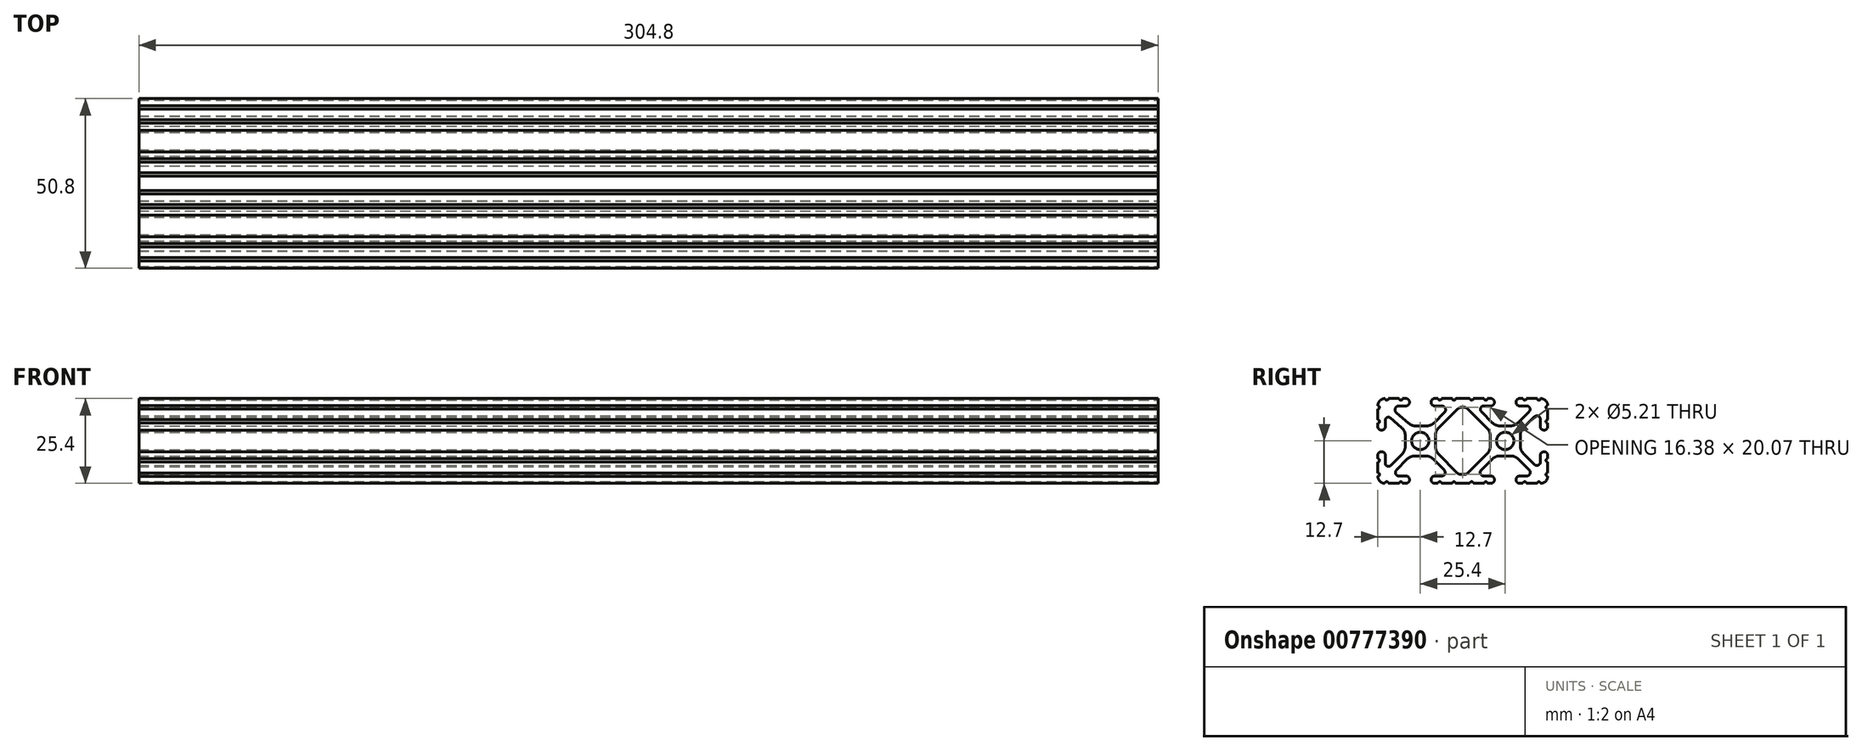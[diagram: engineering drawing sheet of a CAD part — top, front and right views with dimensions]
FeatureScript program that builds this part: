
annotation { "Feature Type Name" : "Feature", "Feature Type Description" : "" }
export const myFeature = defineFeature(function(context is Context, id is Id, definition is map)
    precondition{}
    {
        {
            var Q0;
            Q0=qCreatedBy(makeId("Right.planeOp"),FACE);
            var sketch = newSketch(context, id + "F0", { "sketchPlane" : qUnion([Q0])});
            skLineSegment(sketch, "E0", {"start": v(7.26, 3.87) * mm, "end": v(1.55, 9.57) * mm});
            skArc(sketch, "E1", {"start": v(1.55, 9.57) * mm, "mid": v(1.04, 9.91) * mm, "end": v(0.43, 10.03) * mm});
            skLineSegment(sketch, "E2", {"start": v(0.43, 10.03) * mm, "end": v(-0.43, 10.03) * mm});
            skArc(sketch, "E3", {"start": v(-0.43, 10.03) * mm, "mid": v(-1.04, 9.91) * mm, "end": v(-1.55, 9.57) * mm});
            skLineSegment(sketch, "E4", {"start": v(-1.55, 9.57) * mm, "end": v(-7.26, 3.87) * mm});
            skArc(sketch, "E5", {"start": v(-7.26, 3.87) * mm, "mid": v(-7.95, 2.84) * mm, "end": v(-8.2, 1.62) * mm});
            skLineSegment(sketch, "E6", {"start": v(-8.2, 1.62) * mm, "end": v(-8.2, -1.62) * mm});
            skLineSegment(sketch, "E7", {"start": v(-7.28, -3.85) * mm, "end": v(-1.68, -9.56) * mm});
            skArc(sketch, "E8", {"start": v(-1.68, -9.56) * mm, "mid": v(-1.16, -9.91) * mm, "end": v(-0.55, -10.03) * mm});
            skLineSegment(sketch, "E9", {"start": v(-0.55, -10.03) * mm, "end": v(0.4, -10.03) * mm});
            skArc(sketch, "E10", {"start": v(0.4, -10.03) * mm, "mid": v(1, -9.91) * mm, "end": v(1.5, -9.58) * mm});
            skLineSegment(sketch, "E11", {"start": v(1.5, -9.58) * mm, "end": v(7.25, -3.88) * mm});
            skArc(sketch, "E12", {"start": v(7.25, -3.88) * mm, "mid": v(7.95, -2.84) * mm, "end": v(8.2, -1.62) * mm});
            skLineSegment(sketch, "E13", {"start": v(8.2, -1.62) * mm, "end": v(8.2, 1.62) * mm});
            skArc(sketch, "E14", {"start": v(8.2, 1.62) * mm, "mid": v(7.95, 2.84) * mm, "end": v(7.26, 3.87) * mm});
            skCircle(sketch, "E15", {"center": v(12.7, 0) * mm, "radius": 2.6 * mm});
            skCircle(sketch, "E16", {"center": v(-12.7, 0) * mm, "radius": 2.6 * mm});
            skArc(sketch, "E17", {"start": v(-8.2, -1.62) * mm, "mid": v(-7.96, -2.82) * mm, "end": v(-7.28, -3.85) * mm});
            skLineSegment(sketch, "E18", {"start": v(-15.94, -11.65) * mm, "end": v(-15.94, -11.54) * mm});
            skArc(sketch, "E19", {"start": v(-15.94, -11.54) * mm, "mid": v(-16.25, -10.8) * mm, "end": v(-16.99, -10.5) * mm});
            skLineSegment(sketch, "E20", {"start": v(-16.99, -10.5) * mm, "end": v(-19.12, -10.5) * mm});
            skArc(sketch, "E21", {"start": v(-19.84, -8.77) * mm, "mid": v(-20.05, -9.87) * mm, "end": v(-19.12, -10.5) * mm});
            skLineSegment(sketch, "E22", {"start": v(-19.84, -8.77) * mm, "end": v(-16.62, -5.46) * mm});
            skArc(sketch, "E23", {"start": v(-14.34, -4.5) * mm, "mid": v(-15.58, -4.75) * mm, "end": v(-16.62, -5.46) * mm});
            skLineSegment(sketch, "E24", {"start": v(-14.34, -4.5) * mm, "end": v(-11.08, -4.5) * mm});
            skArc(sketch, "E25", {"start": v(-8.82, -5.45) * mm, "mid": v(-9.85, -4.74) * mm, "end": v(-11.08, -4.5) * mm});
            skLineSegment(sketch, "E26", {"start": v(-8.82, -5.45) * mm, "end": v(-5.56, -8.76) * mm});
            skArc(sketch, "E27", {"start": v(-6.29, -10.5) * mm, "mid": v(-5.35, -9.87) * mm, "end": v(-5.56, -8.76) * mm});
            skLineSegment(sketch, "E28", {"start": v(-6.29, -10.5) * mm, "end": v(-8.41, -10.5) * mm});
            skArc(sketch, "E29", {"start": v(-8.41, -10.5) * mm, "mid": v(-9.15, -10.8) * mm, "end": v(-9.46, -11.54) * mm});
            skLineSegment(sketch, "E30", {"start": v(-9.46, -11.54) * mm, "end": v(-9.46, -11.65) * mm});
            skArc(sketch, "E31", {"start": v(-9.46, -11.65) * mm, "mid": v(-9.15, -12.4) * mm, "end": v(-8.41, -12.7) * mm});
            skLineSegment(sketch, "E32", {"start": v(-8.41, -12.7) * mm, "end": v(-7.38, -12.7) * mm});
            skArc(sketch, "E33", {"start": v(-6.37, -12.7) * mm, "mid": v(-6.87, -12.2) * mm, "end": v(-7.38, -12.7) * mm});
            skLineSegment(sketch, "E34", {"start": v(-6.37, -12.7) * mm, "end": v(-3.15, -12.7) * mm});
            skArc(sketch, "E35", {"start": v(-2.13, -12.7) * mm, "mid": v(-2.64, -12.2) * mm, "end": v(-3.15, -12.7) * mm});
            skLineSegment(sketch, "E36", {"start": v(-2.13, -12.7) * mm, "end": v(2.13, -12.7) * mm});
            skArc(sketch, "E37", {"start": v(3.15, -12.7) * mm, "mid": v(2.64, -12.2) * mm, "end": v(2.13, -12.7) * mm});
            skLineSegment(sketch, "E38", {"start": v(3.15, -12.7) * mm, "end": v(6.37, -12.7) * mm});
            skArc(sketch, "E39", {"start": v(7.38, -12.7) * mm, "mid": v(6.87, -12.2) * mm, "end": v(6.37, -12.7) * mm});
            skLineSegment(sketch, "E40", {"start": v(7.38, -12.7) * mm, "end": v(8.41, -12.7) * mm});
            skArc(sketch, "E41", {"start": v(8.41, -12.7) * mm, "mid": v(9.15, -12.4) * mm, "end": v(9.46, -11.65) * mm});
            skLineSegment(sketch, "E42", {"start": v(9.46, -11.65) * mm, "end": v(9.46, -11.54) * mm});
            skArc(sketch, "E43", {"start": v(9.46, -11.54) * mm, "mid": v(9.15, -10.8) * mm, "end": v(8.41, -10.5) * mm});
            skLineSegment(sketch, "E44", {"start": v(8.41, -10.5) * mm, "end": v(6.28, -10.5) * mm});
            skArc(sketch, "E45", {"start": v(5.53, -8.67) * mm, "mid": v(5.3, -9.83) * mm, "end": v(6.28, -10.5) * mm});
            skLineSegment(sketch, "E46", {"start": v(5.53, -8.67) * mm, "end": v(8.8, -5.42) * mm});
            skArc(sketch, "E47", {"start": v(11.05, -4.5) * mm, "mid": v(9.84, -4.73) * mm, "end": v(8.8, -5.42) * mm});
            skLineSegment(sketch, "E48", {"start": v(11.05, -4.5) * mm, "end": v(14.35, -4.5) * mm});
            skArc(sketch, "E49", {"start": v(16.6, -5.42) * mm, "mid": v(15.56, -4.73) * mm, "end": v(14.35, -4.5) * mm});
            skLineSegment(sketch, "E50", {"start": v(16.6, -5.42) * mm, "end": v(19.87, -8.67) * mm});
            skArc(sketch, "E51", {"start": v(19.12, -10.5) * mm, "mid": v(20.1, -9.83) * mm, "end": v(19.87, -8.67) * mm});
            skLineSegment(sketch, "E52", {"start": v(19.12, -10.5) * mm, "end": v(16.99, -10.5) * mm});
            skArc(sketch, "E53", {"start": v(16.99, -10.5) * mm, "mid": v(16.25, -10.8) * mm, "end": v(15.94, -11.54) * mm});
            skLineSegment(sketch, "E54", {"start": v(15.94, -11.54) * mm, "end": v(15.94, -11.65) * mm});
            skArc(sketch, "E55", {"start": v(15.94, -11.65) * mm, "mid": v(16.25, -12.4) * mm, "end": v(16.99, -12.7) * mm});
            skLineSegment(sketch, "E56", {"start": v(16.99, -12.7) * mm, "end": v(18.02, -12.7) * mm});
            skArc(sketch, "E57", {"start": v(19.03, -12.7) * mm, "mid": v(18.53, -12.2) * mm, "end": v(18.02, -12.7) * mm});
            skLineSegment(sketch, "E58", {"start": v(19.03, -12.7) * mm, "end": v(22.25, -12.7) * mm});
            skArc(sketch, "E59", {"start": v(23.27, -12.7) * mm, "mid": v(22.76, -12.2) * mm, "end": v(22.25, -12.7) * mm});
            skArc(sketch, "E60", {"start": v(23.27, -12.7) * mm, "mid": v(24.78, -12.08) * mm, "end": v(25.4, -10.57) * mm});
            skArc(sketch, "E61", {"start": v(25.4, -9.55) * mm, "mid": v(24.9, -10.06) * mm, "end": v(25.4, -10.57) * mm});
            skLineSegment(sketch, "E62", {"start": v(25.4, -9.55) * mm, "end": v(25.4, -6.33) * mm});
            skArc(sketch, "E63", {"start": v(25.4, -5.32) * mm, "mid": v(24.9, -5.83) * mm, "end": v(25.4, -6.33) * mm});
            skLineSegment(sketch, "E64", {"start": v(25.4, -5.32) * mm, "end": v(25.4, -4.24) * mm});
            skArc(sketch, "E65", {"start": v(25.4, -4.24) * mm, "mid": v(25.1, -3.53) * mm, "end": v(24.4, -3.24) * mm});
            skLineSegment(sketch, "E66", {"start": v(24.4, -3.24) * mm, "end": v(24.24, -3.24) * mm});
            skArc(sketch, "E67", {"start": v(24.24, -3.24) * mm, "mid": v(23.5, -3.55) * mm, "end": v(23.2, -4.29) * mm});
            skLineSegment(sketch, "E68", {"start": v(23.2, -4.29) * mm, "end": v(23.2, -6.33) * mm});
            skArc(sketch, "E69", {"start": v(21.43, -7.07) * mm, "mid": v(22.56, -7.29) * mm, "end": v(23.2, -6.33) * mm});
            skLineSegment(sketch, "E70", {"start": v(21.43, -7.07) * mm, "end": v(18.15, -3.8) * mm});
            skArc(sketch, "E71", {"start": v(17.2, -1.55) * mm, "mid": v(17.45, -2.77) * mm, "end": v(18.15, -3.8) * mm});
            skLineSegment(sketch, "E72", {"start": v(17.2, -1.55) * mm, "end": v(17.2, 1.7) * mm});
            skArc(sketch, "E73", {"start": v(18.14, 3.94) * mm, "mid": v(17.45, 2.91) * mm, "end": v(17.2, 1.7) * mm});
            skLineSegment(sketch, "E74", {"start": v(18.14, 3.94) * mm, "end": v(21.43, 7.23) * mm});
            skArc(sketch, "E75", {"start": v(23.2, 6.5) * mm, "mid": v(22.55, 7.45) * mm, "end": v(21.43, 7.23) * mm});
            skLineSegment(sketch, "E76", {"start": v(23.2, 6.5) * mm, "end": v(23.2, 4.29) * mm});
            skArc(sketch, "E77", {"start": v(23.2, 4.29) * mm, "mid": v(23.5, 3.55) * mm, "end": v(24.24, 3.24) * mm});
            skLineSegment(sketch, "E78", {"start": v(24.24, 3.24) * mm, "end": v(24.35, 3.24) * mm});
            skArc(sketch, "E79", {"start": v(24.35, 3.24) * mm, "mid": v(25.1, 3.55) * mm, "end": v(25.4, 4.29) * mm});
            skLineSegment(sketch, "E80", {"start": v(25.4, 4.29) * mm, "end": v(25.4, 5.32) * mm});
            skArc(sketch, "E81", {"start": v(25.4, 6.33) * mm, "mid": v(24.9, 5.83) * mm, "end": v(25.4, 5.32) * mm});
            skLineSegment(sketch, "E82", {"start": v(25.4, 6.33) * mm, "end": v(25.4, 9.55) * mm});
            skArc(sketch, "E83", {"start": v(25.4, 10.57) * mm, "mid": v(24.9, 10.06) * mm, "end": v(25.4, 9.55) * mm});
            skArc(sketch, "E84", {"start": v(25.4, 10.57) * mm, "mid": v(24.78, 12.08) * mm, "end": v(23.27, 12.7) * mm});
            skArc(sketch, "E85", {"start": v(22.25, 12.7) * mm, "mid": v(22.76, 12.2) * mm, "end": v(23.27, 12.7) * mm});
            skLineSegment(sketch, "E86", {"start": v(22.25, 12.7) * mm, "end": v(19.03, 12.7) * mm});
            skArc(sketch, "E87", {"start": v(18.02, 12.7) * mm, "mid": v(18.53, 12.2) * mm, "end": v(19.03, 12.7) * mm});
            skLineSegment(sketch, "E88", {"start": v(18.02, 12.7) * mm, "end": v(16.99, 12.7) * mm});
            skArc(sketch, "E89", {"start": v(16.99, 12.7) * mm, "mid": v(16.25, 12.4) * mm, "end": v(15.94, 11.65) * mm});
            skLineSegment(sketch, "E90", {"start": v(15.94, 11.65) * mm, "end": v(15.94, 11.54) * mm});
            skArc(sketch, "E91", {"start": v(15.94, 11.54) * mm, "mid": v(16.25, 10.8) * mm, "end": v(16.99, 10.5) * mm});
            skLineSegment(sketch, "E92", {"start": v(16.99, 10.5) * mm, "end": v(19.12, 10.5) * mm});
            skArc(sketch, "E93", {"start": v(19.83, 8.76) * mm, "mid": v(20.06, 9.86) * mm, "end": v(19.12, 10.5) * mm});
            skLineSegment(sketch, "E94", {"start": v(19.83, 8.76) * mm, "end": v(16.5, 5.42) * mm});
            skArc(sketch, "E95", {"start": v(14.25, 4.5) * mm, "mid": v(15.47, 4.74) * mm, "end": v(16.5, 5.42) * mm});
            skLineSegment(sketch, "E96", {"start": v(14.25, 4.5) * mm, "end": v(11.15, 4.5) * mm});
            skArc(sketch, "E97", {"start": v(8.9, 5.42) * mm, "mid": v(9.93, 4.74) * mm, "end": v(11.15, 4.5) * mm});
            skLineSegment(sketch, "E98", {"start": v(8.9, 5.42) * mm, "end": v(5.57, 8.76) * mm});
            skArc(sketch, "E99", {"start": v(6.28, 10.5) * mm, "mid": v(5.34, 9.86) * mm, "end": v(5.57, 8.76) * mm});
            skLineSegment(sketch, "E100", {"start": v(6.28, 10.5) * mm, "end": v(8.41, 10.5) * mm});
            skArc(sketch, "E101", {"start": v(8.41, 10.5) * mm, "mid": v(9.15, 10.8) * mm, "end": v(9.46, 11.54) * mm});
            skLineSegment(sketch, "E102", {"start": v(9.46, 11.54) * mm, "end": v(9.46, 11.65) * mm});
            skArc(sketch, "E103", {"start": v(9.46, 11.65) * mm, "mid": v(9.15, 12.4) * mm, "end": v(8.41, 12.7) * mm});
            skLineSegment(sketch, "E104", {"start": v(8.41, 12.7) * mm, "end": v(7.38, 12.7) * mm});
            skArc(sketch, "E105", {"start": v(6.37, 12.7) * mm, "mid": v(6.87, 12.2) * mm, "end": v(7.38, 12.7) * mm});
            skLineSegment(sketch, "E106", {"start": v(6.37, 12.7) * mm, "end": v(3.15, 12.7) * mm});
            skArc(sketch, "E107", {"start": v(2.13, 12.7) * mm, "mid": v(2.64, 12.2) * mm, "end": v(3.15, 12.7) * mm});
            skLineSegment(sketch, "E108", {"start": v(2.13, 12.7) * mm, "end": v(-2.13, 12.7) * mm});
            skArc(sketch, "E109", {"start": v(-3.15, 12.7) * mm, "mid": v(-2.64, 12.2) * mm, "end": v(-2.13, 12.7) * mm});
            skLineSegment(sketch, "E110", {"start": v(-3.15, 12.7) * mm, "end": v(-6.37, 12.7) * mm});
            skArc(sketch, "E111", {"start": v(-7.38, 12.7) * mm, "mid": v(-6.87, 12.2) * mm, "end": v(-6.37, 12.7) * mm});
            skLineSegment(sketch, "E112", {"start": v(-7.38, 12.7) * mm, "end": v(-8.41, 12.7) * mm});
            skArc(sketch, "E113", {"start": v(-8.41, 12.7) * mm, "mid": v(-9.15, 12.4) * mm, "end": v(-9.46, 11.65) * mm});
            skLineSegment(sketch, "E114", {"start": v(-9.46, 11.65) * mm, "end": v(-9.46, 11.54) * mm});
            skArc(sketch, "E115", {"start": v(-9.46, 11.54) * mm, "mid": v(-9.15, 10.8) * mm, "end": v(-8.41, 10.5) * mm});
            skLineSegment(sketch, "E116", {"start": v(-8.41, 10.5) * mm, "end": v(-6.29, 10.5) * mm});
            skArc(sketch, "E117", {"start": v(-5.48, 8.54) * mm, "mid": v(-5.23, 9.78) * mm, "end": v(-6.29, 10.5) * mm});
            skLineSegment(sketch, "E118", {"start": v(-5.48, 8.54) * mm, "end": v(-8.6, 5.42) * mm});
            skArc(sketch, "E119", {"start": v(-10.84, 4.5) * mm, "mid": v(-9.63, 4.74) * mm, "end": v(-8.6, 5.42) * mm});
            skLineSegment(sketch, "E120", {"start": v(-10.84, 4.5) * mm, "end": v(-14.1, 4.5) * mm});
            skArc(sketch, "E121", {"start": v(-16.19, 5.28) * mm, "mid": v(-15.22, 4.7) * mm, "end": v(-14.1, 4.5) * mm});
            skLineSegment(sketch, "E122", {"start": v(-16.19, 5.28) * mm, "end": v(-19.87, 8.48) * mm});
            skArc(sketch, "E123", {"start": v(-19.12, 10.5) * mm, "mid": v(-20.19, 9.75) * mm, "end": v(-19.87, 8.48) * mm});
            skLineSegment(sketch, "E124", {"start": v(-19.12, 10.5) * mm, "end": v(-16.99, 10.5) * mm});
            skArc(sketch, "E125", {"start": v(-16.99, 10.5) * mm, "mid": v(-16.25, 10.8) * mm, "end": v(-15.94, 11.54) * mm});
            skLineSegment(sketch, "E126", {"start": v(-15.94, 11.54) * mm, "end": v(-15.94, 11.65) * mm});
            skArc(sketch, "E127", {"start": v(-15.94, 11.65) * mm, "mid": v(-16.25, 12.4) * mm, "end": v(-16.99, 12.7) * mm});
            skLineSegment(sketch, "E128", {"start": v(-16.99, 12.7) * mm, "end": v(-18.02, 12.7) * mm});
            skArc(sketch, "E129", {"start": v(-19.03, 12.7) * mm, "mid": v(-18.53, 12.2) * mm, "end": v(-18.02, 12.7) * mm});
            skLineSegment(sketch, "E130", {"start": v(-19.03, 12.7) * mm, "end": v(-22.25, 12.7) * mm});
            skArc(sketch, "E131", {"start": v(-23.27, 12.7) * mm, "mid": v(-22.76, 12.2) * mm, "end": v(-22.25, 12.7) * mm});
            skArc(sketch, "E132", {"start": v(-23.27, 12.7) * mm, "mid": v(-24.78, 12.08) * mm, "end": v(-25.4, 10.57) * mm});
            skArc(sketch, "E133", {"start": v(-25.4, 9.55) * mm, "mid": v(-24.9, 10.06) * mm, "end": v(-25.4, 10.57) * mm});
            skLineSegment(sketch, "E134", {"start": v(-25.4, 9.55) * mm, "end": v(-25.4, 6.33) * mm});
            skArc(sketch, "E135", {"start": v(-25.4, 5.32) * mm, "mid": v(-24.9, 5.83) * mm, "end": v(-25.4, 6.33) * mm});
            skLineSegment(sketch, "E136", {"start": v(-25.4, 5.32) * mm, "end": v(-25.4, 4.24) * mm});
            skArc(sketch, "E137", {"start": v(-25.4, 4.24) * mm, "mid": v(-25.1, 3.53) * mm, "end": v(-24.4, 3.24) * mm});
            skLineSegment(sketch, "E138", {"start": v(-24.4, 3.24) * mm, "end": v(-24.19, 3.24) * mm});
            skArc(sketch, "E139", {"start": v(-24.19, 3.24) * mm, "mid": v(-23.48, 3.53) * mm, "end": v(-23.2, 4.24) * mm});
            skLineSegment(sketch, "E140", {"start": v(-23.2, 4.24) * mm, "end": v(-23.2, 6.16) * mm});
            skArc(sketch, "E141", {"start": v(-21.58, 6.89) * mm, "mid": v(-22.62, 7.04) * mm, "end": v(-23.2, 6.16) * mm});
            skLineSegment(sketch, "E142", {"start": v(-21.58, 6.89) * mm, "end": v(-18.3, 4.02) * mm});
            skArc(sketch, "E143", {"start": v(-17.2, 1.63) * mm, "mid": v(-17.5, 2.95) * mm, "end": v(-18.3, 4.02) * mm});
            skLineSegment(sketch, "E144", {"start": v(-17.2, 1.63) * mm, "end": v(-17.2, -1.63) * mm});
            skArc(sketch, "E145", {"start": v(-18.1, -3.85) * mm, "mid": v(-17.44, -2.83) * mm, "end": v(-17.2, -1.63) * mm});
            skLineSegment(sketch, "E146", {"start": v(-18.1, -3.85) * mm, "end": v(-21.53, -7.35) * mm});
            skArc(sketch, "E147", {"start": v(-23.2, -6.68) * mm, "mid": v(-22.59, -7.57) * mm, "end": v(-21.53, -7.35) * mm});
            skLineSegment(sketch, "E148", {"start": v(-23.2, -6.68) * mm, "end": v(-23.2, -4.24) * mm});
            skArc(sketch, "E149", {"start": v(-23.2, -4.24) * mm, "mid": v(-23.48, -3.53) * mm, "end": v(-24.19, -3.24) * mm});
            skLineSegment(sketch, "E150", {"start": v(-24.19, -3.24) * mm, "end": v(-24.4, -3.24) * mm});
            skArc(sketch, "E151", {"start": v(-24.4, -3.24) * mm, "mid": v(-25.1, -3.53) * mm, "end": v(-25.4, -4.24) * mm});
            skLineSegment(sketch, "E152", {"start": v(-25.4, -4.24) * mm, "end": v(-25.4, -5.32) * mm});
            skArc(sketch, "E153", {"start": v(-25.4, -6.33) * mm, "mid": v(-24.9, -5.83) * mm, "end": v(-25.4, -5.32) * mm});
            skLineSegment(sketch, "E154", {"start": v(-25.4, -6.33) * mm, "end": v(-25.4, -9.55) * mm});
            skArc(sketch, "E155", {"start": v(-25.4, -10.57) * mm, "mid": v(-24.9, -10.06) * mm, "end": v(-25.4, -9.55) * mm});
            skArc(sketch, "E156", {"start": v(-25.4, -10.57) * mm, "mid": v(-24.78, -12.08) * mm, "end": v(-23.27, -12.7) * mm});
            skArc(sketch, "E157", {"start": v(-22.25, -12.7) * mm, "mid": v(-22.76, -12.2) * mm, "end": v(-23.27, -12.7) * mm});
            skLineSegment(sketch, "E158", {"start": v(-22.25, -12.7) * mm, "end": v(-19.03, -12.7) * mm});
            skArc(sketch, "E159", {"start": v(-18.02, -12.7) * mm, "mid": v(-18.53, -12.2) * mm, "end": v(-19.03, -12.7) * mm});
            skLineSegment(sketch, "E160", {"start": v(-18.02, -12.7) * mm, "end": v(-16.99, -12.7) * mm});
            skArc(sketch, "E161", {"start": v(-16.99, -12.7) * mm, "mid": v(-16.25, -12.4) * mm, "end": v(-15.94, -11.65) * mm});
            skSolve(sketch);
        }
        {
            var Q0;
            Q0=qSketchRegion(id+"F0",true);
            extrude(context, id + "F1", {"entities" : qUnion([Q0]), "oppositeDirection" : true, "depth" : 304.8 * mm, "offsetDistance" : 25.4 * mm});
        }
    });
